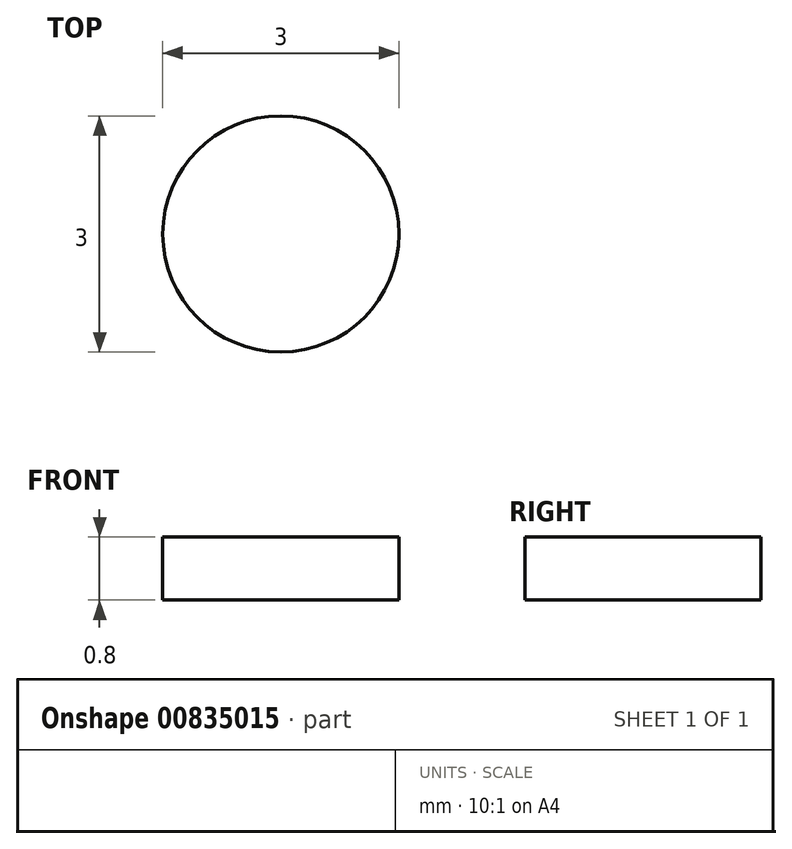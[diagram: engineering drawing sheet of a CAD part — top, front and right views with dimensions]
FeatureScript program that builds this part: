
annotation { "Feature Type Name" : "Feature", "Feature Type Description" : "" }
export const myFeature = defineFeature(function(context is Context, id is Id, definition is map)
    precondition{}
    {
        {
            var Q0;
            Q0=qCreatedBy(makeId("Top.planeOp"),FACE);
            var sketch = newSketch(context, id + "F0", { "sketchPlane" : qUnion([Q0])});
            skCircle(sketch, "E0", {"center": v(0, 0) * mm, "radius": 1.5 * mm});
            skSolve(sketch);
        }
        {
            var Q0;
            Q0 = qSketchRegion(id + "F0", true);
            extrude(context, id + "F1", {"entities" : qUnion([Q0]), "depth" : .8 * mm, "offsetDistance" : 25 * mm});
        }
    });
